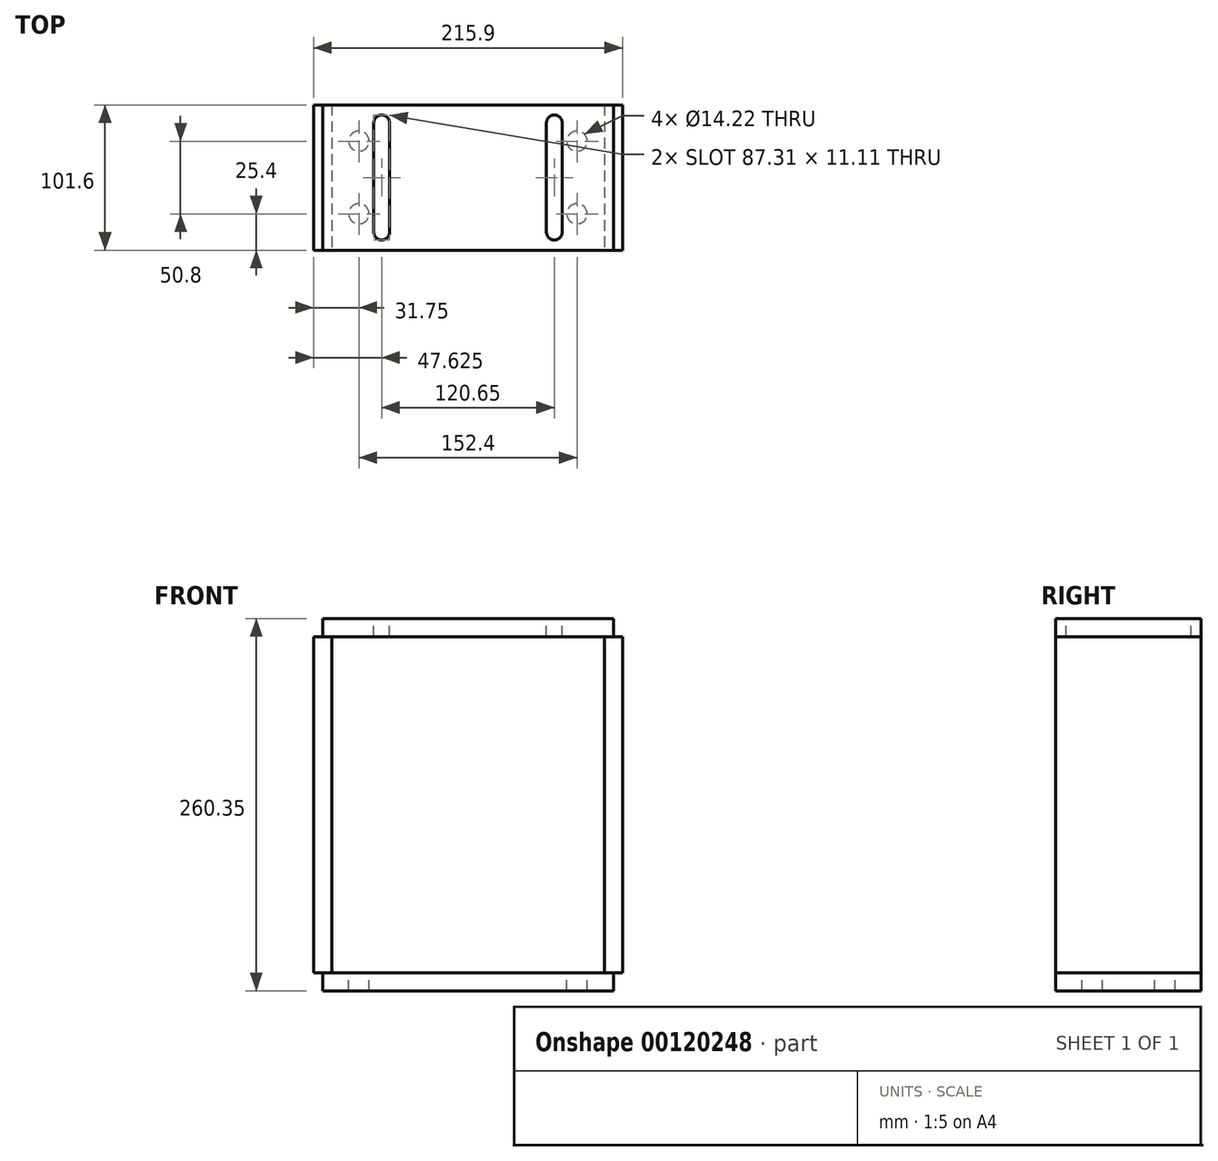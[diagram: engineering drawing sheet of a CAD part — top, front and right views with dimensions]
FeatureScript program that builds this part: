
annotation { "Feature Type Name" : "Feature", "Feature Type Description" : "" }
export const myFeature = defineFeature(function(context is Context, id is Id, definition is map)
    precondition{}
    {
        {
            var Q0;
            Q0=qCreatedBy(makeId("Top.planeOp"),FACE);
            var sketch = newSketch(context, id + "F0", { "sketchPlane" : qUnion([Q0])});
            skLineSegment(sketch, "E0.rect.bottom", {"start": v(-101.6, 50.8) * mm, "end": v(101.6, 50.8) * mm});
            skLineSegment(sketch, "E0.rect.top", {"start": v(-101.6, -50.8) * mm, "end": v(101.6, -50.8) * mm});
            skLineSegment(sketch, "E0.rect.left", {"start": v(-101.6, 50.8) * mm, "end": v(-101.6, -50.8) * mm});
            skLineSegment(sketch, "E0.rect.right", {"start": v(101.6, 50.8) * mm, "end": v(101.6, -50.8) * mm});
            skPoint(sketch, "E0.rect.middle", {"position": v(0, 0) * mm});
            skLineSegment(sketch, "E1.0", {"start": v(-76.2, 25.4) * mm, "end": v(76.2, 25.4) * mm, "construction": true});
            skLineSegment(sketch, "E1.1", {"start": v(-76.2, 25.4) * mm, "end": v(-76.2, -25.4) * mm, "construction": true});
            skLineSegment(sketch, "E1.2", {"start": v(-76.2, -25.4) * mm, "end": v(76.2, -25.4) * mm, "construction": true});
            skLineSegment(sketch, "E1.3", {"start": v(76.2, 25.4) * mm, "end": v(76.2, -25.4) * mm, "construction": true});
            skPoint(sketch, "E2", {"position": v(-76.2, 25.4) * mm});
            skPoint(sketch, "E3", {"position": v(76.2, 25.4) * mm});
            skPoint(sketch, "E4", {"position": v(76.2, -25.4) * mm});
            skPoint(sketch, "E5", {"position": v(-76.2, -25.4) * mm});
            skSolve(sketch);
        }
        {
            var Q0;
            Q0=qSketchRegion(id+"F0",true);
            extrude(context, id + "F1", {"entities" : qUnion([Q0]), "oppositeDirection" : true, "depth" : 12.7 * mm});
        }
        {
            var Q0;
            Q0=sQuery(id+"F0.wireOp",VERTEX,"E2");
            var Q1;
            Q1=sQuery(id+"F0.wireOp",VERTEX,"E3");
            var Q2;
            Q2=sQuery(id+"F0.wireOp",VERTEX,"E4");
            var Q3;
            Q3=sQuery(id+"F0.wireOp",VERTEX,"E5");
            var Q4;
            Q4=makeQuery(id+"F1.opExtrude","SWEPT_BODY",BODY,{"disambiguationData":[OSD([sQuery(id+"F0.wireOp",EDGE,"E0.rect.bottom"),sQuery(id+"F0.wireOp",EDGE,"E0.rect.top"),sQuery(id+"F0.wireOp",EDGE,"E0.rect.left"),sQuery(id+"F0.wireOp",EDGE,"E0.rect.right")])]});
            hole(context, id + "F2", {"style" : HoleStyle.SIMPLE, "holeDiameter" : 14.22 * mm, "endStyle" : HoleEndStyle.THROUGH, "locations" : qUnion([Q0, Q1, Q2, Q3]), "scope" : qUnion([Q4])});
        }
        {
            var Q0;
            Q0=makeQuery(id+"F1.opExtrude","CAP_FACE",FACE,{"disambiguationData":[OSD([sQuery(id+"F0.wireOp",EDGE,"E0.rect.bottom"),sQuery(id+"F0.wireOp",EDGE,"E0.rect.top"),sQuery(id+"F0.wireOp",EDGE,"E0.rect.left"),sQuery(id+"F0.wireOp",EDGE,"E0.rect.right")])],"isStart":false});
            cPlane(context, id + "F3", {"entities" : qUnion([Q0]), "cplaneType" : CPlaneType.OFFSET, "offset" : 260.35 * mm, "oppositeDirection" : true, "width" : 152.4 * mm, "height" : 152.4 * mm});
        }
        {
            var Q0;
            Q0=qCreatedBy(id+"F3.planeOp",FACE);
            var sketch = newSketch(context, id + "F4", { "sketchPlane" : qUnion([Q0])});
            skLineSegment(sketch, "E6.0", {"start": v(-101.6, -50.8) * mm, "end": v(101.6, -50.8) * mm});
            skLineSegment(sketch, "E7.0", {"start": v(101.6, -50.8) * mm, "end": v(101.6, 50.8) * mm});
            skLineSegment(sketch, "E8.0", {"start": v(-101.6, 50.8) * mm, "end": v(101.6, 50.8) * mm});
            skLineSegment(sketch, "E9.0", {"start": v(-101.6, -50.8) * mm, "end": v(-101.6, 50.8) * mm});
            skSolve(sketch);
        }
        {
            var Q0;
            Q0=qSketchRegion(id+"F4",true);
            extrude(context, id + "F5", {"entities" : qUnion([Q0]), "depth" : 12.7 * mm});
        }
        {
            var Q0;
            Q0=makeQuery(id+"F5.opExtrude","CAP_FACE",FACE,{"disambiguationData":[OSD([sQuery(id+"F4.wireOp",EDGE,"E6.0"),sQuery(id+"F4.wireOp",EDGE,"E7.0"),sQuery(id+"F4.wireOp",EDGE,"E8.0"),sQuery(id+"F4.wireOp",EDGE,"E9.0")])],"isStart":true});
            var sketch = newSketch(context, id + "F6", { "sketchPlane" : qUnion([Q0])});
            skLineSegment(sketch, "E10", {"start": v(-101.6, 0) * mm, "end": v(101.6, 0) * mm, "construction": true});
            skLineSegment(sketch, "E11", {"start": v(0, 50.8) * mm, "end": v(0, -50.8) * mm, "construction": true});
            skLineSegment(sketch, "E12.0", {"start": v(-60.32, 76.2) * mm, "end": v(-60.33, -76.2) * mm, "construction": true});
            skLineSegment(sketch, "E13.0", {"start": v(-101.6, 19.81) * mm, "end": v(101.6, 19.81) * mm, "construction": true});
            skPoint(sketch, "E14", {"position": v(-60.32, 19.81) * mm});
            skPoint(sketch, "E15.MirrorP", {"position": v(-60.32, -19.81) * mm});
            skPoint(sketch, "E16.MirrorP", {"position": v(60.32, 19.81) * mm});
            skPoint(sketch, "E17.MirrorP", {"position": v(60.32, -19.81) * mm});
            skLineSegment(sketch, "E18", {"start": v(-60.32, 12.7) * mm, "end": v(-60.32, 38.1) * mm});
            skArc(sketch, "E19.0.startCap", {"start": v(-54.77, 12.7) * mm, "mid": v(-60.32, 7.14) * mm, "end": v(-65.88, 12.7) * mm});
            skArc(sketch, "E19.0.endCap", {"start": v(-65.88, 38.1) * mm, "mid": v(-60.33, 43.66) * mm, "end": v(-54.77, 38.1) * mm});
            skLineSegment(sketch, "E19.0.left", {"start": v(-65.88, 12.7) * mm, "end": v(-65.88, 38.1) * mm});
            skLineSegment(sketch, "E19.0.right", {"start": v(-54.77, -12.7) * mm, "end": v(-54.77, 38.1) * mm});
            skLineSegment(sketch, "E20.MirrorCS", {"start": v(-65.88, 12.7) * mm, "end": v(-65.88, -38.1) * mm});
            skLineSegment(sketch, "E21.MirrorCS", {"start": v(-54.77, -12.7) * mm, "end": v(-54.77, -38.1) * mm});
            skLineSegment(sketch, "E22.MirrorCS", {"start": v(-60.32, -12.7) * mm, "end": v(-60.32, -38.1) * mm});
            skArc(sketch, "E23.MirrorCS", {"start": v(-65.88, -38.1) * mm, "mid": v(-60.32, -43.66) * mm, "end": v(-54.77, -38.1) * mm});
            skArc(sketch, "E24.MirrorCS", {"start": v(-54.77, -12.7) * mm, "mid": v(-60.32, -7.14) * mm, "end": v(-65.88, -12.7) * mm});
            skArc(sketch, "E25.MirrorCS", {"start": v(54.77, -12.7) * mm, "mid": v(60.32, -7.14) * mm, "end": v(65.88, -12.7) * mm});
            skArc(sketch, "E26.MirrorCS", {"start": v(54.77, 12.7) * mm, "mid": v(60.33, 7.14) * mm, "end": v(65.88, 12.7) * mm});
            skLineSegment(sketch, "E27.MirrorCS", {"start": v(65.88, -12.7) * mm, "end": v(65.88, -38.1) * mm});
            skLineSegment(sketch, "E28.MirrorCS", {"start": v(60.32, 12.7) * mm, "end": v(60.33, 38.1) * mm});
            skArc(sketch, "E29.MirrorCS", {"start": v(65.88, -38.1) * mm, "mid": v(60.32, -43.66) * mm, "end": v(54.77, -38.1) * mm});
            skLineSegment(sketch, "E30.MirrorCS", {"start": v(54.77, -12.7) * mm, "end": v(54.77, -38.1) * mm});
            skLineSegment(sketch, "E31.MirrorCS", {"start": v(60.32, -12.7) * mm, "end": v(60.32, -38.1) * mm});
            skArc(sketch, "E32.MirrorCS", {"start": v(65.88, 38.1) * mm, "mid": v(60.32, 43.66) * mm, "end": v(54.77, 38.1) * mm});
            skLineSegment(sketch, "E33.MirrorCS", {"start": v(65.88, -12.7) * mm, "end": v(65.88, 38.1) * mm});
            skLineSegment(sketch, "E34.MirrorCS", {"start": v(54.77, -12.7) * mm, "end": v(54.77, 38.1) * mm});
            skSolve(sketch);
        }
        {
            var Q0;
            Q0=qSketchRegion(id+"F6",true);
            extrude(context, id + "F7", {"entities" : qUnion([Q0]), "operationType" : NewBodyOperationType.REMOVE, "oppositeDirection" : true, "depth" : 25.4 * mm});
        }
        {
            var Q0;
            Q0=makeQuery(id+"F5.opExtrude","SWEPT_FACE",FACE,{"disambiguationData":[OSD([sQuery(id+"F4.wireOp",EDGE,"E7.0")])]});
            var sketch = newSketch(context, id + "F8", { "sketchPlane" : qUnion([Q0])});
            skLineSegment(sketch, "E35.0", {"start": v(50.8, 234.95) * mm, "end": v(-50.8, 234.95) * mm});
            skLineSegment(sketch, "E36.0", {"start": v(50.8, 0) * mm, "end": v(-50.8, 0) * mm});
            skLineSegment(sketch, "E37", {"start": v(-50.8, 234.95) * mm, "end": v(-50.8, 0) * mm});
            skLineSegment(sketch, "E38", {"start": v(50.8, 234.95) * mm, "end": v(50.8, 0) * mm});
            skSolve(sketch);
        }
        {
            var Q0;
            Q0 = qSketchRegion(id + "F8", true);
            extrude(context, id + "F9", {"entities" : qUnion([Q0]), "endBound" : BoundingType.SYMMETRIC, "depth" : 12.7 * mm});
        }
        {
            var Q0;
            Q0=makeQuery(id+"F9.opExtrude","SWEPT_BODY",BODY,{"disambiguationData":[OSD([sQuery(id+"F8.wireOp",EDGE,"E35.0"),sQuery(id+"F8.wireOp",EDGE,"E36.0"),sQuery(id+"F8.wireOp",EDGE,"E37"),sQuery(id+"F8.wireOp",EDGE,"E38")])]});
            var Q1;
            Q1=qCreatedBy(makeId("Right.planeOp"),FACE);
            mirror(context, id + "F10", {"entities" : qUnion([Q0]), "mirrorPlane" : qUnion([Q1])});
        }
    });
